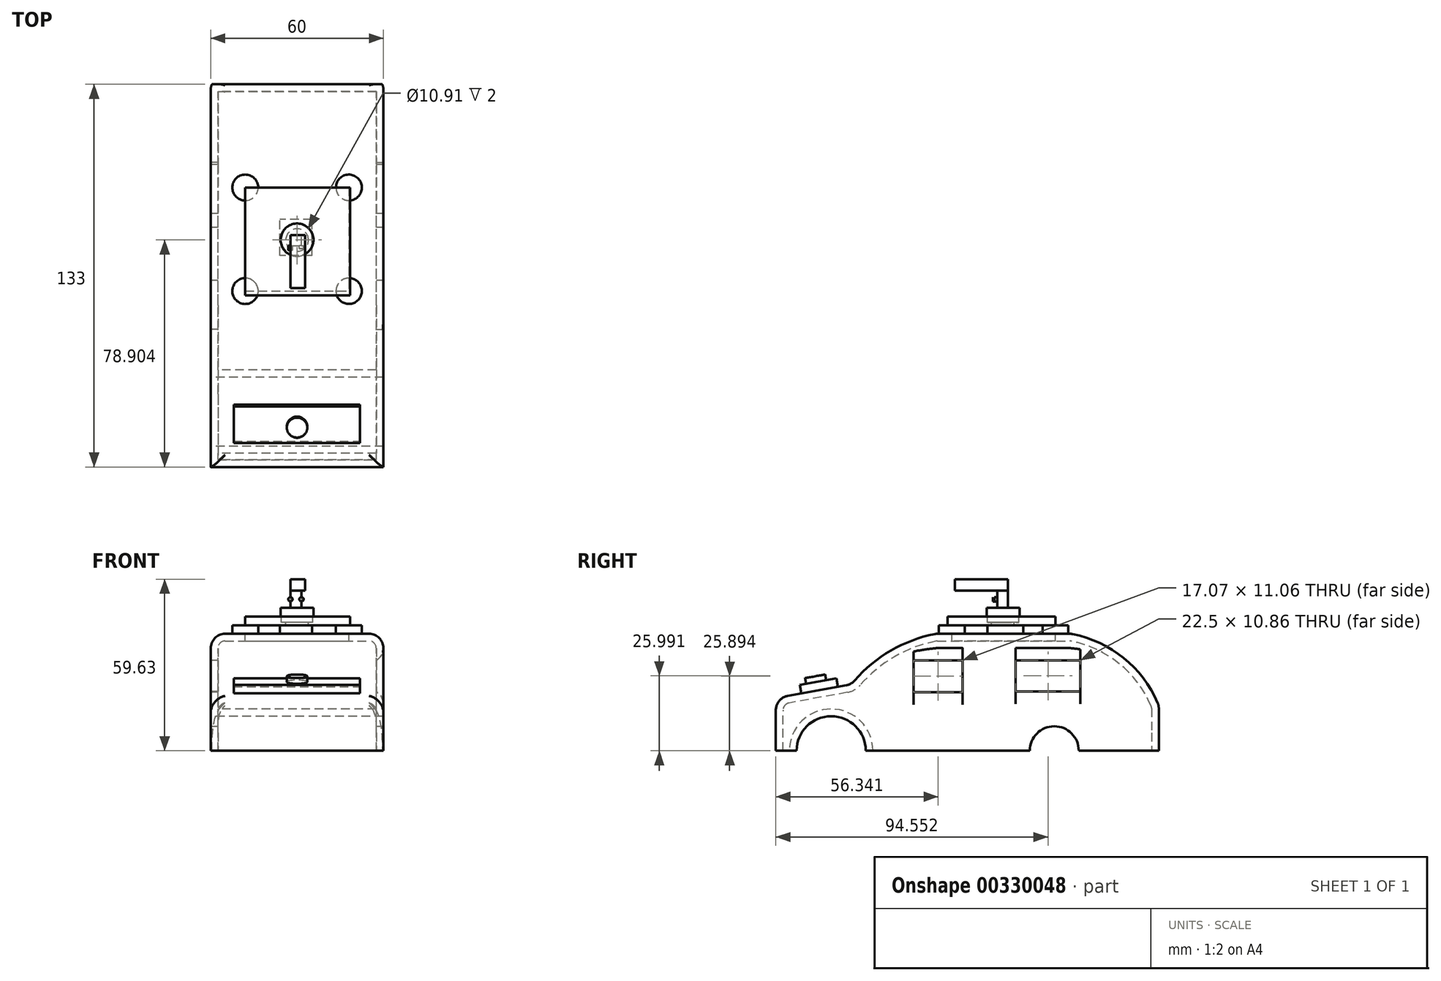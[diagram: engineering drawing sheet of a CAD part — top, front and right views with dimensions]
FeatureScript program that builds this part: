
annotation { "Feature Type Name" : "Feature", "Feature Type Description" : "" }
export const myFeature = defineFeature(function(context is Context, id is Id, definition is map)
    precondition{}
    {
        {
            var Q0;
            Q0=qCreatedBy(makeId("Right.planeOp"),FACE);
            var sketch = newSketch(context, id + "F0", { "sketchPlane" : qUnion([Q0])});
            skLineSegment(sketch, "E0", {"start": v(-62.16, 0) * mm, "end": v(70.84, 0) * mm});
            skLineSegment(sketch, "E1", {"start": v(70.84, 0) * mm, "end": v(70.84, 40.63) * mm});
            skLineSegment(sketch, "E2", {"start": v(-62.16, 0) * mm, "end": v(-62.16, 40.63) * mm});
            skLineSegment(sketch, "E3", {"start": v(-62.16, 40.63) * mm, "end": v(70.84, 40.63) * mm});
            skLineSegment(sketch, "E4", {"start": v(-62.16, 40.63) * mm, "end": v(-62.16, 40.63) * mm});
            skLineSegment(sketch, "E5", {"start": v(-62.16, 40.63) * mm, "end": v(-62.16, 0) * mm});
            skCircle(sketch, "E6", {"center": v(-42.95, 0) * mm, "radius": 12 * mm});
            skCircle(sketch, "E7", {"center": v(28.24, 2) * mm, "radius": 12 * mm});
            skLineSegment(sketch, "E8", {"start": v(-62.16, 18.3) * mm, "end": v(-35.88, 23.08) * mm});
            skArc(sketch, "E9", {"start": v(-6.49, 40.63) * mm, "mid": v(-22.76, 34.5) * mm, "end": v(-35.88, 23.08) * mm});
            skArc(sketch, "E10", {"start": v(70.84, 15.71) * mm, "mid": v(58.83, 32.06) * mm, "end": v(40.44, 40.63) * mm});
            skSolve(sketch);
        }
        {
            var Q0;
            {var subQ0=sQuery(id+"F0.wireOp",EDGE,"E6");var subQ1=sQuery(id+"F0.wireOp",EDGE,"E0");var subQ2=makeQuery(id+"F0.imprint","INTERSECT",VERTEX,{"disambiguationData":[OD(0.0)],"derivedFrom":[subQ1,subQ0]});Q0=makeQuery(id+"F0.imprint","IMPRINT",FACE,{"disambiguationData":[TD([[makeQuery(id+"F0.imprint","IMPRINT",EDGE,{"disambiguationData":[TD([[subQ2,-1.0]])],"derivedFrom":subQ1}),1.0]])]});}
            var Q1;
            {var subQ0=sQuery(id+"F0.wireOp",EDGE,"E7");var subQ1=sQuery(id+"F0.wireOp",EDGE,"E0");var subQ2=makeQuery(id+"F0.imprint","INTERSECT",VERTEX,{"disambiguationData":[OD(0.0)],"derivedFrom":[subQ1,subQ0]});Q1=makeQuery(id+"F0.imprint","IMPRINT",FACE,{"disambiguationData":[TD([[makeQuery(id+"F0.imprint","IMPRINT",EDGE,{"disambiguationData":[TD([[subQ2,-1.0]])],"derivedFrom":subQ1}),1.0]])]});}
            var Q2;
            {var subQ9=sQuery(id+"F0.wireOp",EDGE,"E8");Q2=makeQuery(id+"F0.imprint","IMPRINT",FACE,{"disambiguationData":[TD([[makeQuery(id+"F0.imprint","IMPRINT",EDGE,{"derivedFrom":subQ9}),-1.0]])]});}
            extrude(context, id + "F1", {"entities" : qUnion([Q0, Q1, Q2]), "endBound" : BoundingType.SYMMETRIC, "depth" : 60 * mm});
        }
        {
            var Q0;
            Q0=makeQuery(id+"F1.opExtrude","CAP_EDGE",EDGE,{"disambiguationData":[OSD([sQuery(id+"F0.wireOp",EDGE,"E3")])],"isStart":false});
            var Q1;
            Q1=makeQuery(id+"F1.opExtrude","CAP_EDGE",EDGE,{"disambiguationData":[OSD([sQuery(id+"F0.wireOp",EDGE,"E9")])],"isStart":false});
            var Q2;
            Q2=makeQuery(id+"F1.opExtrude","CAP_EDGE",EDGE,{"disambiguationData":[OSD([sQuery(id+"F0.wireOp",EDGE,"E3")])],"isStart":true});
            var Q3;
            Q3=makeQuery(id+"F1.opExtrude","CAP_EDGE",EDGE,{"disambiguationData":[OSD([sQuery(id+"F0.wireOp",EDGE,"E9")])],"isStart":true});
            var Q4;
            Q4=makeQuery(id+"F1.opExtrude","CAP_EDGE",EDGE,{"disambiguationData":[OSD([sQuery(id+"F0.wireOp",EDGE,"E8")])],"isStart":true});
            var Q5;
            Q5=makeQuery(id+"F1.opExtrude","SWEPT_EDGE",EDGE,{"disambiguationData":[OSD([sQuery(id+"F0.wireOp",EDGE,"E5"),sQuery(id+"F0.wireOp",EDGE,"E8")])]});
            var Q6;
            Q6=makeQuery(id+"F1.opExtrude","CAP_EDGE",EDGE,{"disambiguationData":[OSD([sQuery(id+"F0.wireOp",EDGE,"E8")])],"isStart":false});
            var Q7;
            Q7=makeQuery(id+"F1.opExtrude","CAP_EDGE",EDGE,{"disambiguationData":[OSD([sQuery(id+"F0.wireOp",EDGE,"E10")])],"isStart":false});
            var Q8;
            Q8=makeQuery(id+"F1.opExtrude","CAP_EDGE",EDGE,{"disambiguationData":[OSD([sQuery(id+"F0.wireOp",EDGE,"E10")])],"isStart":true});
            var Q9;
            Q9=makeQuery(id+"F1.opExtrude","SWEPT_EDGE",EDGE,{"disambiguationData":[OSD([sQuery(id+"F0.wireOp",EDGE,"E3"),sQuery(id+"F0.wireOp",EDGE,"E9")])]});
            var Q10;
            Q10=makeQuery(id+"F1.opExtrude","SWEPT_EDGE",EDGE,{"disambiguationData":[OSD([sQuery(id+"F0.wireOp",EDGE,"E8"),sQuery(id+"F0.wireOp",EDGE,"E9")])]});
            var Q11;
            Q11=makeQuery(id+"F1.opExtrude","SWEPT_EDGE",EDGE,{"disambiguationData":[OSD([sQuery(id+"F0.wireOp",EDGE,"E3"),sQuery(id+"F0.wireOp",EDGE,"E10")])]});
            var Q12;
            Q12=makeQuery(id+"F1.opExtrude","CAP_EDGE",EDGE,{"disambiguationData":[OSD([sQuery(id+"F0.wireOp",EDGE,"E5")])],"isStart":true});
            var Q13;
            Q13=makeQuery(id+"F1.opExtrude","CAP_EDGE",EDGE,{"disambiguationData":[OSD([sQuery(id+"F0.wireOp",EDGE,"E5")])],"isStart":false});
            var Q14;
            Q14=makeQuery(id+"F1.opExtrude","SWEPT_EDGE",EDGE,{"disambiguationData":[OSD([sQuery(id+"F0.wireOp",EDGE,"E1"),sQuery(id+"F0.wireOp",EDGE,"E10")])]});
            fillet(context, id + "F2", {"entities" : qUnion([Q0, Q1, Q2, Q3, Q4, Q5, Q6, Q7, Q8, Q9, Q10, Q11, Q12, Q13, Q14]), "radius" : 5 * mm, "tangentPropagation" : true, "allowEdgeOverflow" : false});
        }
        {
            var Q0;
            Q0=makeQuery(id+"F1.opExtrude","SWEPT_FACE",FACE,{"disambiguationData":[OSD([sQuery(id+"F0.wireOp",EDGE,"E0")])]});
            shell(context, id + "F3", {"entities" : qUnion([Q0]), "thickness" : 2.5 * mm});
        }
        {
            var Q0;
            Q0=makeQuery(id+"F1.opExtrude","CAP_FACE",FACE,{"disambiguationData":[OSD([sQuery(id+"F0.wireOp",EDGE,"E0"),sQuery(id+"F0.wireOp",EDGE,"E1"),sQuery(id+"F0.wireOp",EDGE,"E3"),sQuery(id+"F0.wireOp",EDGE,"E5"),sQuery(id+"F0.wireOp",EDGE,"E8"),sQuery(id+"F0.wireOp",EDGE,"E9"),sQuery(id+"F0.wireOp",EDGE,"E10")])],"isStart":true});
            var sketch = newSketch(context, id + "F4", { "sketchPlane" : qUnion([Q0])});
            skLineSegment(sketch, "E11", {"start": v(17.2, 31.84) * mm, "end": v(17.2, 26.51) * mm});
            skSolve(sketch);
        }
        {
            var Q0;
            Q0=makeQuery(id+"F1.opExtrude","CAP_FACE",FACE,{"disambiguationData":[OSD([sQuery(id+"F0.wireOp",EDGE,"E0"),sQuery(id+"F0.wireOp",EDGE,"E1"),sQuery(id+"F0.wireOp",EDGE,"E3"),sQuery(id+"F0.wireOp",EDGE,"E5"),sQuery(id+"F0.wireOp",EDGE,"E8"),sQuery(id+"F0.wireOp",EDGE,"E9"),sQuery(id+"F0.wireOp",EDGE,"E10")])],"isStart":false});
            var sketch = newSketch(context, id + "F5", { "sketchPlane" : qUnion([Q0])});
            skCircle(sketch, "E12", {"center": v(-41.1, 0) * mm, "radius": 8.5 * mm});
            skCircle(sketch, "E13", {"center": v(34.55, 0) * mm, "radius": 8.5 * mm});
            skSolve(sketch);
        }
        {
            var Q0;
            Q0 = qSketchRegion(id + "F5", true);
            extrude(context, id + "F6", {"entities" : qUnion([Q0]), "operationType" : NewBodyOperationType.REMOVE, "endBound" : BoundingType.THROUGH_ALL, "oppositeDirection" : true, "depth" : 25 * mm});
        }
        {
            var Q0;
            {var subQ5=sQuery(id+"F0.wireOp",EDGE,"E0");Q0=makeQuery(id+"F4.imprint","IMPRINT",FACE,{"disambiguationData":[TD([[makeQuery(id+"F4.imprint","IMPRINT",EDGE,{"derivedFrom":makeQuery(id+"F1.opExtrude","CAP_EDGE",EDGE,{"disambiguationData":[OSD([subQ5])],"isStart":true})}),-1.0]])]});}
            var sketch = newSketch(context, id + "F7", { "sketchPlane" : qUnion([Q0])});
            skLineSegment(sketch, "E14.bottom", {"start": v(-43.64, 20.56) * mm, "end": v(-21.14, 20.56) * mm});
            skLineSegment(sketch, "E14.top", {"start": v(-43.64, 31.42) * mm, "end": v(-21.14, 31.42) * mm});
            skLineSegment(sketch, "E14.left", {"start": v(-43.64, 20.56) * mm, "end": v(-43.64, 31.42) * mm});
            skLineSegment(sketch, "E14.right", {"start": v(-21.14, 20.56) * mm, "end": v(-21.14, 31.42) * mm});
            skLineSegment(sketch, "E15.bottom", {"start": v(-2.72, 31.42) * mm, "end": v(14.35, 31.42) * mm});
            skLineSegment(sketch, "E15.top", {"start": v(-2.72, 20.37) * mm, "end": v(14.35, 20.37) * mm});
            skLineSegment(sketch, "E15.left", {"start": v(-2.72, 31.42) * mm, "end": v(-2.72, 20.37) * mm});
            skLineSegment(sketch, "E15.right", {"start": v(14.35, 31.42) * mm, "end": v(14.35, 20.37) * mm});
            skSolve(sketch);
        }
        {
            var Q0;
            Q0 = qSketchRegion(id + "F7", true);
            extrude(context, id + "F8", {"entities" : qUnion([Q0]), "operationType" : NewBodyOperationType.REMOVE, "endBound" : BoundingType.THROUGH_ALL, "oppositeDirection" : true, "depth" : 25 * mm});
        }
        {
            var Q0;
            Q0=makeQuery(id+"F8.boolean.opBoolean","COPY",EDGE,{"derivedFrom":makeQuery(id+"F8.opExtrude","CAP_EDGE",EDGE,{"disambiguationData":[OSD([sQuery(id+"F7.wireOp",EDGE,"E14.top")])],"isStart":true})});
            var Q1;
            Q1=makeQuery(id+"F8.boolean.opBoolean","COPY",EDGE,{"derivedFrom":makeQuery(id+"F8.opExtrude","CAP_EDGE",EDGE,{"disambiguationData":[OSD([sQuery(id+"F7.wireOp",EDGE,"E14.bottom")])],"isStart":true})});
            var Q2;
            {var subQ0=sQuery(id+"F0.wireOp",EDGE,"E9");Q2=makeQuery(id+"F3.opShell","OFFSET_FACE",FACE,{"disambiguationData":[OSD([subQ0]),TDD([makeQuery(id+"F2.opFillet","BLEND_FACE",FACE,{"disambiguationData":[OSD([subQ0]),TDD([makeQuery(id+"F1.opExtrude","CAP_EDGE",EDGE,{"disambiguationData":[OSD([subQ0])],"isStart":false})])]})])]});}
            var Q3;
            {var subQ0=sQuery(id+"F0.wireOp",EDGE,"E9");var subQ1=sQuery(id+"F0.wireOp",EDGE,"E8");Q3=makeQuery(id+"F3.opShell","OFFSET_EDGE",EDGE,{"disambiguationData":[OSD([subQ1,subQ0]),TDD([makeQuery(id+"F2.opFillet","BLEND_EDGE",EDGE,{"blendedFrom":[makeQuery(id+"F1.opExtrude","SWEPT_EDGE",EDGE,{"disambiguationData":[OSD([subQ1,subQ0])]}),makeQuery(id+"F1.opExtrude","SWEPT_FACE",FACE,{"disambiguationData":[OSD([subQ0])]})],"blendedInto":[makeQuery(id+"F1.opExtrude","SWEPT_FACE",FACE,{"disambiguationData":[OSD([subQ0])]})]})])]});}
            var Q4;
            Q4=makeQuery(id+"F8.boolean.opBoolean","COPY",EDGE,{"derivedFrom":makeQuery(id+"F8.opExtrude","CAP_EDGE",EDGE,{"disambiguationData":[OSD([sQuery(id+"F7.wireOp",EDGE,"E15.top")])],"isStart":true})});
            var Q5;
            Q5=makeQuery(id+"F8.boolean.opBoolean","COPY",EDGE,{"derivedFrom":makeQuery(id+"F8.opExtrude","CAP_EDGE",EDGE,{"disambiguationData":[OSD([sQuery(id+"F7.wireOp",EDGE,"E15.bottom")])],"isStart":true})});
            var Q6;
            {var subQ0=sQuery(id+"F0.wireOp",EDGE,"E9");Q6=makeQuery(id+"F3.opShell","OFFSET_EDGE",EDGE,{"disambiguationData":[OSD([subQ0]),TDD([makeQuery(id+"F2.opFillet","BLEND_EDGE",EDGE,{"blendedFrom":[makeQuery(id+"F1.opExtrude","CAP_EDGE",EDGE,{"disambiguationData":[OSD([subQ0])],"isStart":false}),makeQuery(id+"F1.opExtrude","SWEPT_FACE",FACE,{"disambiguationData":[OSD([subQ0])]})],"blendedInto":[makeQuery(id+"F1.opExtrude","SWEPT_FACE",FACE,{"disambiguationData":[OSD([subQ0])]})]})])]});}
            var Q7;
            {var subQ0=sQuery(id+"F0.wireOp",EDGE,"E10");var subQ1=sQuery(id+"F0.wireOp",EDGE,"E9");var subQ2=sQuery(id+"F0.wireOp",EDGE,"E8");var subQ3=sQuery(id+"F0.wireOp",EDGE,"E5");var subQ4=sQuery(id+"F0.wireOp",EDGE,"E3");var subQ5=sQuery(id+"F0.wireOp",EDGE,"E1");var subQ6=sQuery(id+"F0.wireOp",EDGE,"E0");Q7=makeQuery(id+"F3.opShell","OFFSET_EDGE",EDGE,{"disambiguationData":[OSD([subQ6,subQ5,subQ4,subQ3,subQ2,subQ1,subQ0]),TDD([makeQuery(id+"F2.opFillet","BLEND_EDGE",EDGE,{"blendedFrom":[makeQuery(id+"F1.opExtrude","CAP_EDGE",EDGE,{"disambiguationData":[OSD([subQ1])],"isStart":false}),makeQuery(id+"F1.opExtrude","CAP_FACE",FACE,{"disambiguationData":[OSD([subQ6,subQ5,subQ4,subQ3,subQ2,subQ1,subQ0])],"isStart":false})],"blendedInto":[makeQuery(id+"F1.opExtrude","CAP_FACE",FACE,{"disambiguationData":[OSD([subQ6,subQ5,subQ4,subQ3,subQ2,subQ1,subQ0])],"isStart":false})]})])]});}
            var Q8;
            Q8=makeQuery(id+"F8.boolean.opBoolean","INTERSECT",EDGE,{"derivedFrom":[makeQuery(id+"F1.opExtrude","CAP_FACE",FACE,{"disambiguationData":[OSD([sQuery(id+"F0.wireOp",EDGE,"E0"),sQuery(id+"F0.wireOp",EDGE,"E1"),sQuery(id+"F0.wireOp",EDGE,"E3"),sQuery(id+"F0.wireOp",EDGE,"E5"),sQuery(id+"F0.wireOp",EDGE,"E8"),sQuery(id+"F0.wireOp",EDGE,"E9"),sQuery(id+"F0.wireOp",EDGE,"E10")])],"isStart":false}),makeQuery(id+"F8.opExtrude","SWEPT_FACE",FACE,{"disambiguationData":[OSD([sQuery(id+"F7.wireOp",EDGE,"E15.bottom")])]})]});
            var Q9;
            Q9=makeQuery(id+"F8.boolean.opBoolean","INTERSECT",EDGE,{"derivedFrom":[makeQuery(id+"F1.opExtrude","CAP_FACE",FACE,{"disambiguationData":[OSD([sQuery(id+"F0.wireOp",EDGE,"E0"),sQuery(id+"F0.wireOp",EDGE,"E1"),sQuery(id+"F0.wireOp",EDGE,"E3"),sQuery(id+"F0.wireOp",EDGE,"E5"),sQuery(id+"F0.wireOp",EDGE,"E8"),sQuery(id+"F0.wireOp",EDGE,"E9"),sQuery(id+"F0.wireOp",EDGE,"E10")])],"isStart":false}),makeQuery(id+"F8.opExtrude","SWEPT_FACE",FACE,{"disambiguationData":[OSD([sQuery(id+"F7.wireOp",EDGE,"E15.top")])]})]});
            var Q10;
            Q10=makeQuery(id+"F8.boolean.opBoolean","INTERSECT",EDGE,{"derivedFrom":[makeQuery(id+"F1.opExtrude","CAP_FACE",FACE,{"disambiguationData":[OSD([sQuery(id+"F0.wireOp",EDGE,"E0"),sQuery(id+"F0.wireOp",EDGE,"E1"),sQuery(id+"F0.wireOp",EDGE,"E3"),sQuery(id+"F0.wireOp",EDGE,"E5"),sQuery(id+"F0.wireOp",EDGE,"E8"),sQuery(id+"F0.wireOp",EDGE,"E9"),sQuery(id+"F0.wireOp",EDGE,"E10")])],"isStart":false}),makeQuery(id+"F8.opExtrude","SWEPT_FACE",FACE,{"disambiguationData":[OSD([sQuery(id+"F7.wireOp",EDGE,"E14.top")])]})]});
            var Q11;
            Q11=makeQuery(id+"F8.boolean.opBoolean","INTERSECT",EDGE,{"derivedFrom":[makeQuery(id+"F1.opExtrude","CAP_FACE",FACE,{"disambiguationData":[OSD([sQuery(id+"F0.wireOp",EDGE,"E0"),sQuery(id+"F0.wireOp",EDGE,"E1"),sQuery(id+"F0.wireOp",EDGE,"E3"),sQuery(id+"F0.wireOp",EDGE,"E5"),sQuery(id+"F0.wireOp",EDGE,"E8"),sQuery(id+"F0.wireOp",EDGE,"E9"),sQuery(id+"F0.wireOp",EDGE,"E10")])],"isStart":false}),makeQuery(id+"F8.opExtrude","SWEPT_FACE",FACE,{"disambiguationData":[OSD([sQuery(id+"F7.wireOp",EDGE,"E14.bottom")])]})]});
            fillet(context, id + "F9", {"entities" : qUnion([Q0, Q1, Q2, Q3, Q4, Q5, Q6, Q7, Q8, Q9, Q10, Q11]), "radius" : 5 * mm, "tangentPropagation" : true, "allowEdgeOverflow" : false});
        }
        {
            var Q0;
            Q0=makeQuery(id+"F1.opExtrude","SWEPT_FACE",FACE,{"disambiguationData":[OSD([sQuery(id+"F0.wireOp",EDGE,"E8")])]});
            var sketch = newSketch(context, id + "F10", { "sketchPlane" : qUnion([Q0])});
            skLineSegment(sketch, "E16.bottom", {"start": v(-22, -35.92) * mm, "end": v(21.82, -35.92) * mm});
            skLineSegment(sketch, "E16.top", {"start": v(-22, -48.83) * mm, "end": v(21.82, -48.83) * mm});
            skLineSegment(sketch, "E16.left", {"start": v(-22, -35.92) * mm, "end": v(-22, -48.83) * mm});
            skLineSegment(sketch, "E16.right", {"start": v(21.82, -35.92) * mm, "end": v(21.82, -48.83) * mm});
            skSolve(sketch);
        }
        {
            var Q0;
            Q0 = qSketchRegion(id + "F10", true);
            extrude(context, id + "F11", {"entities" : qUnion([Q0]), "operationType" : NewBodyOperationType.ADD, "depth" : 3 * mm});
        }
        {
            var Q0;
            Q0=makeQuery(id+"F11.opExtrude","CAP_FACE",FACE,{"disambiguationData":[OSD([sQuery(id+"F10.wireOp",EDGE,"E16.bottom"),sQuery(id+"F10.wireOp",EDGE,"E16.top"),sQuery(id+"F10.wireOp",EDGE,"E16.left"),sQuery(id+"F10.wireOp",EDGE,"E16.right")])],"isStart":false});
            var sketch = newSketch(context, id + "F12", { "sketchPlane" : qUnion([Q0])});
            skCircle(sketch, "E17", {"center": v(0, -43.1) * mm, "radius": 3.54 * mm});
            skSolve(sketch);
        }
        {
            var Q0;
            Q0 = qSketchRegion(id + "F12", true);
            extrude(context, id + "F13", {"entities" : qUnion([Q0]), "operationType" : NewBodyOperationType.ADD, "depth" : 2 * mm});
        }
        {
            var Q0;
            Q0=makeQuery(id+"F1.opExtrude","SWEPT_FACE",FACE,{"disambiguationData":[OSD([sQuery(id+"F0.wireOp",EDGE,"E3")])]});
            var sketch = newSketch(context, id + "F14", { "sketchPlane" : qUnion([Q0])});
            skLineSegment(sketch, "E18.bottom", {"start": v(-18, 34.96) * mm, "end": v(18, 34.96) * mm});
            skLineSegment(sketch, "E18.top", {"start": v(-18, -1.02) * mm, "end": v(18, -1.02) * mm});
            skLineSegment(sketch, "E18.left", {"start": v(-18, 34.96) * mm, "end": v(-18, -1.02) * mm});
            skLineSegment(sketch, "E18.right", {"start": v(18, 34.96) * mm, "end": v(18, -1.02) * mm});
            skSolve(sketch);
        }
        {
            var Q0;
            Q0 = qSketchRegion(id + "F14", true);
            extrude(context, id + "F15", {"entities" : qUnion([Q0]), "operationType" : NewBodyOperationType.REMOVE, "oppositeDirection" : true, "depth" : 5 * mm});
        }
        {
            var Q0;
            Q0=makeQuery(id+"F1.opExtrude","SWEPT_FACE",FACE,{"disambiguationData":[OSD([sQuery(id+"F0.wireOp",EDGE,"E3")])]});
            var sketch = newSketch(context, id + "F16", { "sketchPlane" : qUnion([Q0])});
            skCircle(sketch, "E19", {"center": v(-18, 34.96) * mm, "radius": 4.5 * mm});
            skCircle(sketch, "E20", {"center": v(18, 34.96) * mm, "radius": 4.5 * mm});
            skCircle(sketch, "E21", {"center": v(18, -1.02) * mm, "radius": 4.5 * mm});
            skCircle(sketch, "E22", {"center": v(-18, -1.02) * mm, "radius": 4.5 * mm});
            skSolve(sketch);
        }
        {
            var Q0;
            Q0 = qSketchRegion(id + "F16", true);
            extrude(context, id + "F17", {"entities" : qUnion([Q0]), "operationType" : NewBodyOperationType.ADD, "depth" : 3 * mm});
        }
        {
            var Q0;
            Q0=makeQuery(id+"F17.opExtrude","CAP_FACE",FACE,{"disambiguationData":[OSD([sQuery(id+"F16.wireOp",EDGE,"E19")])],"isStart":false});
            var sketch = newSketch(context, id + "F18", { "sketchPlane" : qUnion([Q0])});
            skLineSegment(sketch, "E23.bottom", {"start": v(-18, 34.96) * mm, "end": v(18.39, 34.96) * mm});
            skLineSegment(sketch, "E23.top", {"start": v(-18, -2.49) * mm, "end": v(18.39, -2.49) * mm});
            skLineSegment(sketch, "E23.left", {"start": v(-18, 34.96) * mm, "end": v(-18, -2.49) * mm});
            skLineSegment(sketch, "E23.right", {"start": v(18.39, 34.96) * mm, "end": v(18.39, -2.49) * mm});
            skSolve(sketch);
        }
        {
            var Q0;
            Q0 = qSketchRegion(id + "F18", true);
            extrude(context, id + "F19", {"entities" : qUnion([Q0]), "operationType" : NewBodyOperationType.ADD, "depth" : 3 * mm});
        }
        {
            var Q0;
            Q0=makeQuery(id+"F19.opExtrude","CAP_FACE",FACE,{"disambiguationData":[OSD([sQuery(id+"F18.wireOp",EDGE,"E23.bottom"),sQuery(id+"F18.wireOp",EDGE,"E23.top"),sQuery(id+"F18.wireOp",EDGE,"E23.left"),sQuery(id+"F18.wireOp",EDGE,"E23.right")])],"isStart":false});
            var sketch = newSketch(context, id + "F20", { "sketchPlane" : qUnion([Q0])});
            skCircle(sketch, "E24", {"center": v(0, 16.72) * mm, "radius": 3.93 * mm});
            skSolve(sketch);
        }
        {
            var Q0;
            Q0 = qSketchRegion(id + "F20", true);
            extrude(context, id + "F21", {"entities" : qUnion([Q0]), "operationType" : NewBodyOperationType.REMOVE, "oppositeDirection" : true, "depth" : 5 * mm});
        }
        {
            var Q0;
            Q0=makeQuery(id+"F19.opExtrude","CAP_FACE",FACE,{"disambiguationData":[OSD([sQuery(id+"F18.wireOp",EDGE,"E23.bottom"),sQuery(id+"F18.wireOp",EDGE,"E23.top"),sQuery(id+"F18.wireOp",EDGE,"E23.left"),sQuery(id+"F18.wireOp",EDGE,"E23.right")])],"isStart":true});
            var sketch = newSketch(context, id + "F22", { "sketchPlane" : qUnion([Q0])});
            skLineSegment(sketch, "E25.bottom", {"start": v(5.2, -11.3) * mm, "end": v(-5.98, -11.3) * mm});
            skLineSegment(sketch, "E25.top", {"start": v(5.2, -23.82) * mm, "end": v(-5.98, -23.82) * mm});
            skLineSegment(sketch, "E25.left", {"start": v(5.2, -11.3) * mm, "end": v(5.2, -23.82) * mm});
            skLineSegment(sketch, "E25.right", {"start": v(-5.98, -11.3) * mm, "end": v(-5.98, -23.82) * mm});
            skSolve(sketch);
        }
        {
            var Q0;
            Q0 = qSketchRegion(id + "F22", true);
            extrude(context, id + "F23", {"entities" : qUnion([Q0]), "operationType" : NewBodyOperationType.ADD, "depth" : 3 * mm});
        }
        {
            var Q0;
            Q0=makeQuery(id+"F20.imprint","IMPRINT",FACE,{"disambiguationData":[TD([[makeQuery(id+"F20.imprint","IMPRINT",EDGE,{"derivedFrom":sQuery(id+"F20.wireOp",EDGE,"E24")}),-1.0]])]});
            var sketch = newSketch(context, id + "F24", { "sketchPlane" : qUnion([Q0])});
            skCircle(sketch, "E26", {"center": v(0, 16.74) * mm, "radius": 5.46 * mm});
            skSolve(sketch);
        }
        {
            var Q0;
            Q0 = qSketchRegion(id + "F24", true);
            extrude(context, id + "F25", {"entities" : qUnion([Q0]), "operationType" : NewBodyOperationType.REMOVE, "oppositeDirection" : true, "depth" : 2 * mm});
        }
        {
            var Q0;
            Q0=makeQuery(id+"F20.imprint","IMPRINT",FACE,{"disambiguationData":[TD([[makeQuery(id+"F20.imprint","IMPRINT",EDGE,{"derivedFrom":sQuery(id+"F20.wireOp",EDGE,"E24")}),1.0]])]});
            var sketch = newSketch(context, id + "F26", { "sketchPlane" : qUnion([Q0])});
            skCircle(sketch, "E27", {"center": v(0, 16.76) * mm, "radius": 5.7 * mm});
            skSolve(sketch);
        }
        {
            var Q0;
            Q0 = qSketchRegion(id + "F26", true);
            extrude(context, id + "F27", {"entities" : qUnion([Q0]), "operationType" : NewBodyOperationType.ADD, "depth" : 3 * mm});
        }
        {
            var Q0;
            Q0=makeQuery(id+"F27.opExtrude","CAP_FACE",FACE,{"disambiguationData":[OSD([sQuery(id+"F26.wireOp",EDGE,"E27")])],"isStart":false});
            var sketch = newSketch(context, id + "F28", { "sketchPlane" : qUnion([Q0])});
            skLineSegment(sketch, "E28.bottom", {"start": v(-2.32, 14.77) * mm, "end": v(1.54, 14.77) * mm});
            skLineSegment(sketch, "E28.top", {"start": v(-2.32, 18.4) * mm, "end": v(1.54, 18.4) * mm});
            skLineSegment(sketch, "E28.left", {"start": v(-2.32, 14.77) * mm, "end": v(-2.32, 18.4) * mm});
            skLineSegment(sketch, "E28.right", {"start": v(1.54, 14.77) * mm, "end": v(1.54, 18.4) * mm});
            skSolve(sketch);
        }
        {
            var Q0;
            Q0 = qSketchRegion(id + "F28", true);
            extrude(context, id + "F29", {"entities" : qUnion([Q0]), "operationType" : NewBodyOperationType.ADD, "depth" : 6 * mm});
        }
        {
            var Q0;
            Q0=makeQuery(id+"F29.opExtrude","CAP_FACE",FACE,{"disambiguationData":[OSD([sQuery(id+"F28.wireOp",EDGE,"E28.bottom"),sQuery(id+"F28.wireOp",EDGE,"E28.top"),sQuery(id+"F28.wireOp",EDGE,"E28.left"),sQuery(id+"F28.wireOp",EDGE,"E28.right")])],"isStart":false});
            var sketch = newSketch(context, id + "F30", { "sketchPlane" : qUnion([Q0])});
            skLineSegment(sketch, "E29.bottom", {"start": v(-2.32, 18.4) * mm, "end": v(2.77, 18.4) * mm});
            skLineSegment(sketch, "E29.top", {"start": v(-2.32, 0) * mm, "end": v(2.77, 0) * mm});
            skLineSegment(sketch, "E29.left", {"start": v(-2.32, 18.4) * mm, "end": v(-2.32, 0) * mm});
            skLineSegment(sketch, "E29.right", {"start": v(2.77, 18.4) * mm, "end": v(2.77, 0) * mm});
            skSolve(sketch);
        }
        {
            var Q0;
            Q0 = qSketchRegion(id + "F30", true);
            extrude(context, id + "F31", {"entities" : qUnion([Q0]), "operationType" : NewBodyOperationType.ADD, "depth" : 4 * mm});
        }
        {
            var Q0;
            Q0=makeQuery(id+"F29.opExtrude","SWEPT_FACE",FACE,{"disambiguationData":[OSD([sQuery(id+"F28.wireOp",EDGE,"E28.bottom")])]});
            var sketch = newSketch(context, id + "F32", { "sketchPlane" : qUnion([Q0])});
            skCircle(sketch, "E30", {"center": v(-2.32, 52.63) * mm, "radius": 0.75 * mm});
            skSolve(sketch);
        }
        {
            var Q0;
            Q0 = qSketchRegion(id + "F32", true);
            extrude(context, id + "F33", {"entities" : qUnion([Q0]), "operationType" : NewBodyOperationType.ADD, "depth" : 1.5 * mm});
        }
        {
            var Q0;
            Q0=makeQuery(id+"F29.opExtrude","SWEPT_FACE",FACE,{"disambiguationData":[OSD([sQuery(id+"F28.wireOp",EDGE,"E28.bottom")])]});
            var sketch = newSketch(context, id + "F34", { "sketchPlane" : qUnion([Q0])});
            skCircle(sketch, "E31", {"center": v(1.54, 52.63) * mm, "radius": 0.75 * mm});
            skSolve(sketch);
        }
        {
            var Q0;
            Q0 = qSketchRegion(id + "F34", true);
            extrude(context, id + "F35", {"entities" : qUnion([Q0]), "operationType" : NewBodyOperationType.ADD, "depth" : 1 * mm});
        }
    });
